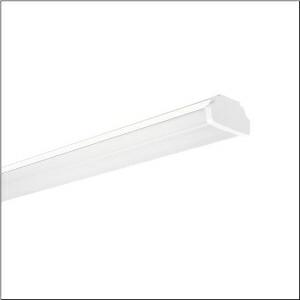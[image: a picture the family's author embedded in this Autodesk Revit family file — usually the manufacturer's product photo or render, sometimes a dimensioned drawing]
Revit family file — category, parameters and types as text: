
# Revit family: modario_r__31_gen_2_53bm812cv685c2_24c7
name_source: partatom
category: Lighting Fixtures
units: mm (PartAtom-declared; Revit-internal decimal feet)

## family parameters
Cut with Voids When Loaded = No
Host = Face
Light Source = No
Part Type = Normal
Room Calculation Point = No
Round Connector Dimension = Use Diameter
Shared = No

## types (1)
- --- (1 x LED, 8970 lm, 49.9 W, 6500K)
    Apparent Load = 50 VA
    CIE Flux Codes = 47 80 95 93 100
    Color Rendering = 80
    Color Temperature = 6500K
    Default Elevation = 1800 mm
    Description = Modario® 31 Gen.2, luminaire insert, of sheet steel, coil coated, white, length: 1.495mm, width: 81mm, height: 82mm, 5x system unit, system units: 299mm, LED rated luminous flux: 8.970lm, light colour: 865, control gear: ON/OFF Multilumen, CLOi, with plug, 3-pole, with phase selection, mains connection: 220..240V, AC, 50/60Hz, start of lifetime: 50W, end of service life: 61W, through-wiring accessed according to module size, primary optical cover: cover, of PMMA, light emission: direct distribution, primary light characteristic: symmetric, protection rating (complete): IP20, protection rating (LED compartment): IP50, insulation class (complete): insulation class I (protective earthing), certification: CE, ENEC, VDE, UKCA, impact resistance: IK03, permissible ambient temperature for indoor applications: -35..+40°C, corresponds to IFS (International Featured Standards) requirements for safety and quality in the food industry, reducing of maximum allowable ambient temperature of 5°C with ceiling mounting, IP40 when using the optional accessory 5TP9018, packaging unit: 1 piece
    Height = 92 mm
    Lamp = 1 x LED
    Lamp Light Flux = 8970 lm
    Lamp Power = 49.9 W
    Lamp count = 1
    Length = 1495 mm
    Luminous efficacy = 180 lm/W
    Manufacturer = Siteco
    ModVariant = No
    Model = 53BM812CV685C2
    Mounting Place = Ceiling
    Mounting Type = Pendant
    Number of Poles = 1
    OnlyDefault = Yes
    Power Factor = 1
    Product Name = Modario® 31 Gen.2
    Product group = luminaire insert | ceiling pendant
    ProductGroupID = 902
    Protection Class = Protection class I
    Protection Degree = IP 20
    RLX_Detail_Level = 1
    RLX_Emergency_Light_Flux = 0 lm
    RLX_Emergency_Type = 0
    RLX_Emergency_Type_DB = No
    RlxData = <blob elided: 40181 chars, md5=299dabea>
    Socket = socket
    Standby Power = 0 W
    System Light Flux = 8970 lm
    System Power = 50 W
    Type Comments = factory setting: luminous flux: 100 % | (A | C | E) | 116 mA
    Type Image = l_1341886.jpg
    URL = http://relux.com
    VarID = @adj_064253
    Voltage = 0 V
    Weight = 0.00 kg
    Width = 81 mm

## geometry (parser evidence)
native form markers: Blend x4, Sweep x11
no freeform markers — native parametric forms only
